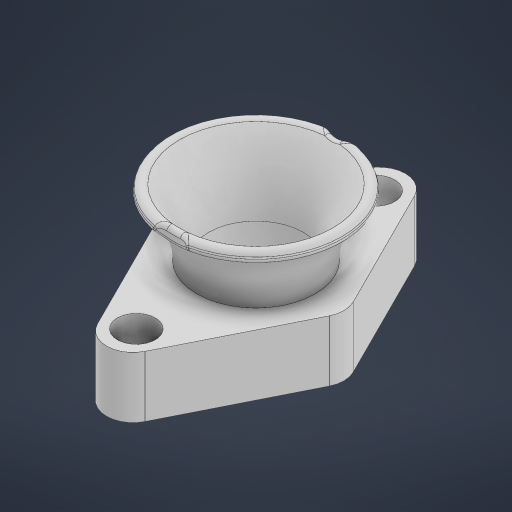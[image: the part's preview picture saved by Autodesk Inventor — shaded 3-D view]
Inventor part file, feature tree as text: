
AUTODESK INVENTOR PART (.ipt)
format: ipt  version: 2024.2 (Build 282272000, 272)  size: 457,728 bytes
history: native  units: mm
features: extrude x5, sketch x4, projected_geometry x3, fillet x2, plane x1, revolve x1
ambient origin geometry x8: Origin, YZ Plane, XZ Plane, XY Plane, X Axis, Y Axis, Z Axis, Center Point
bodies: Solid1 (feature_tree)
feature tree (16):
  sketch  "Sketch1"  dims[d0=12.5mm d1=5.0mm d2=5.0mm]
  extrude  "Extrusion1"  Depth=5.0mm
  fillet  "Fillet1"  Radius=5.0mm
  extrude  "Extrusion2"  Depth=15.75mm
  extrude  "Extrusion3"  Depth=24.0mm
  plane  "Work Plane2"
  extrude  "Extrusion4"  Depth=12.0mm
  revolve  "Revolution1"  [1 undecoded]
  extrude  "Extrusion5"  Depth=3.5mm
  fillet  "Fillet3"  Radius=20.0mm
  sketch  "Sketch2"  dims[d3=15.75mm d4=15.75mm]
  sketch  "Sketch4"  dims[d5=24.0mm d6=24.0mm]
  projected_geometry  "Projected Loop1"
  projected_geometry  "Projected Loop2"
  sketch  "Sketch5"  dims[d7=12.0mm d8=12.0mm d9=8.0mm d10=0.0mm d11=3.5mm d12=20.0mm d13=3.5mm d14=0.0mm d17=10.0mm d18=0.0mm d19=26.451mm d20=10.0mm d21=0.0mm d22=60.0deg d25=90.0deg d26=0.8mm d27=0.4mm d28=10.0mm d29=10.0mm d30=10.0mm d31=0.0mm d32=0.5mm]
  projected_geometry  "Projected Loop3"
note: 1 required parameter value undecoded (feature->parameter linkage not recoverable at this tier; creation-order binding heuristic only, values carry confidence <= 0.55)
